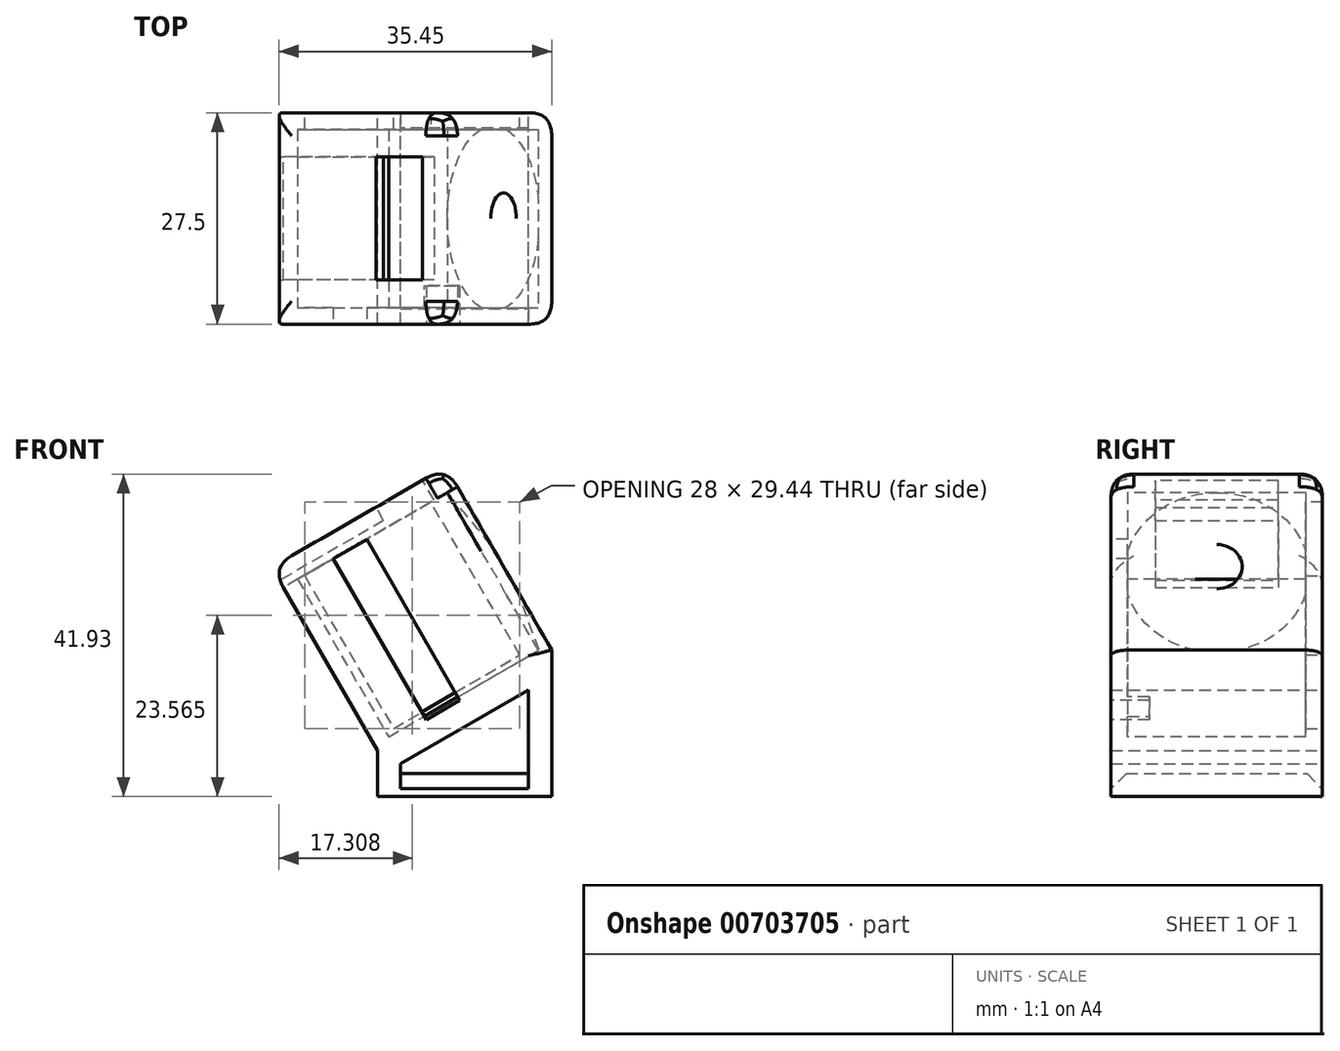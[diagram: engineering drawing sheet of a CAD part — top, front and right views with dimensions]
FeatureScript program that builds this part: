
annotation { "Feature Type Name" : "Feature", "Feature Type Description" : "" }
export const myFeature = defineFeature(function(context is Context, id is Id, definition is map)
    precondition{}
    {
        {
            var Q0;
            Q0=qCreatedBy(makeId("Front.planeOp"),FACE);
            var sketch = newSketch(context, id + "F0", { "sketchPlane" : qUnion([Q0])});
            skLineSegment(sketch, "E0", {"start": v(-14.45, -19.8) * mm, "end": v(8.2, -19.8) * mm});
            skLineSegment(sketch, "E1", {"start": v(-14.45, -19.8) * mm, "end": v(-14.45, -13.8) * mm});
            skLineSegment(sketch, "E2", {"start": v(-14.45, -13.8) * mm, "end": v(8.2, -0.73) * mm});
            skLineSegment(sketch, "E3", {"start": v(8.2, -0.73) * mm, "end": v(8.2, -19.8) * mm});
            skLineSegment(sketch, "E4", {"start": v(5.2, -16.8) * mm, "end": v(-11.45, -16.8) * mm});
            skPoint(sketch, "E4.startSnap0", {"position": v(-14.45, -16.8) * mm});
            skLineSegment(sketch, "E5", {"start": v(-11.45, -16.8) * mm, "end": v(-11.45, -15.53) * mm});
            skLineSegment(sketch, "E6", {"start": v(-11.45, -15.53) * mm, "end": v(5.2, -5.93) * mm});
            skLineSegment(sketch, "E7", {"start": v(5.2, -5.93) * mm, "end": v(5.2, -16.8) * mm});
            skLineSegment(sketch, "E8", {"start": v(-14.45, -13.8) * mm, "end": v(-28.2, 10.01) * mm});
            skLineSegment(sketch, "E9", {"start": v(-28.2, 10.01) * mm, "end": v(-5.55, 23.09) * mm});
            skLineSegment(sketch, "E10", {"start": v(-5.55, 23.09) * mm, "end": v(8.2, -0.73) * mm});
            skLineSegment(sketch, "E11", {"start": v(-28.2, 10.01) * mm, "end": v(-14.45, -13.8) * mm});
            skLineSegment(sketch, "E12", {"start": v(6.68, -1.6) * mm, "end": v(-15.88, -14.63) * mm});
            skSolve(sketch);
        }
        {
            var Q0;
            Q0 = qSketchRegion(id + "F0", true);
            extrude(context, id + "F1", {"entities" : qUnion([Q0]), "endBound" : BoundingType.SYMMETRIC, "depth" : 27.5 * mm, "offsetDistance" : 25 * mm});
        }
        {
            var Q0;
            Q0=qCreatedBy(makeId("Front.planeOp"),FACE);
            var sketch = newSketch(context, id + "F2", { "sketchPlane" : qUnion([Q0])});
            skLineSegment(sketch, "E13", {"start": v(-5.38, 19.72) * mm, "end": v(-24.86, 8.47) * mm});
            skLineSegment(sketch, "E14", {"start": v(-24.86, 8.47) * mm, "end": v(-13.01, -12.05) * mm});
            skLineSegment(sketch, "E15", {"start": v(8.3, 1.03) * mm, "end": v(8.3, 1.03) * mm});
            skLineSegment(sketch, "E16", {"start": v(-13.01, -12.05) * mm, "end": v(6.47, -0.8) * mm});
            skLineSegment(sketch, "E17", {"start": v(-5.38, 19.72) * mm, "end": v(6.47, -0.8) * mm});
            skSolve(sketch);
        }
        {
            var Q0;
            Q0 = qSketchRegion(id + "F2", true);
            extrude(context, id + "F3", {"entities" : qUnion([Q0]), "operationType" : NewBodyOperationType.REMOVE, "endBound" : BoundingType.SYMMETRIC, "oppositeDirection" : true, "depth" : 23.15 * mm, "offsetDistance" : 25 * mm});
        }
        {
            var Q0;
            Q0=makeQuery(id+"F1.opExtrude","SWEPT_FACE",FACE,{"disambiguationData":[OSD([sQuery(id+"F0.wireOp",EDGE,"E9")])]});
            var sketch = newSketch(context, id + "F4", { "sketchPlane" : qUnion([Q0])});
            skLineSegment(sketch, "E18", {"start": v(3.21, 8) * mm, "end": v(3.21, -8) * mm});
            skLineSegment(sketch, "E19", {"start": v(3.21, -8) * mm, "end": v(-3.79, -8) * mm});
            skLineSegment(sketch, "E20", {"start": v(-3.79, -8) * mm, "end": v(-3.79, 8) * mm});
            skLineSegment(sketch, "E21", {"start": v(-3.79, 8) * mm, "end": v(3.21, 8) * mm});
            skSolve(sketch);
        }
        {
            var Q0;
            Q0 = qSketchRegion(id + "F4", true);
            extrude(context, id + "F5", {"entities" : qUnion([Q0]), "operationType" : NewBodyOperationType.REMOVE, "oppositeDirection" : true, "depth" : 5 * mm, "offsetDistance" : 25 * mm});
        }
        {
            var Q0;
            Q0=makeQuery(id+"F1.opExtrude","CAP_FACE",FACE,{"disambiguationData":[OSD([sQuery(id+"F0.wireOp",EDGE,"E0"),sQuery(id+"F0.wireOp",EDGE,"E1"),sQuery(id+"F0.wireOp",EDGE,"E3"),sQuery(id+"F0.wireOp",EDGE,"E4"),sQuery(id+"F0.wireOp",EDGE,"E5"),sQuery(id+"F0.wireOp",EDGE,"E6"),sQuery(id+"F0.wireOp",EDGE,"E7"),sQuery(id+"F0.wireOp",EDGE,"E9"),sQuery(id+"F0.wireOp",EDGE,"E10"),sQuery(id+"F0.wireOp",EDGE,"E11")])],"isStart":false});
            var sketch = newSketch(context, id + "F6", { "sketchPlane" : qUnion([Q0])});
            skLineSegment(sketch, "E22", {"start": v(-20.2, 11.17) * mm, "end": v(-8.1, -9.8) * mm});
            skLineSegment(sketch, "E23", {"start": v(-8.1, -9.8) * mm, "end": v(-3.77, -7.3) * mm});
            skLineSegment(sketch, "E24", {"start": v(-3.77, -7.3) * mm, "end": v(-15.87, 13.67) * mm});
            skLineSegment(sketch, "E25", {"start": v(-15.87, 13.67) * mm, "end": v(-20.2, 11.17) * mm});
            skSolve(sketch);
        }
        {
            var Q0;
            Q0 = qSketchRegion(id + "F6", true);
            extrude(context, id + "F7", {"entities" : qUnion([Q0]), "operationType" : NewBodyOperationType.REMOVE, "oppositeDirection" : true, "depth" : 5 * mm, "offsetDistance" : 25 * mm});
        }
        {
            var Q0;
            Q0=makeQuery(id+"F5.boolean.opBoolean","COPY",EDGE,{"derivedFrom":makeQuery(id+"F5.opExtrude","CAP_EDGE",EDGE,{"disambiguationData":[OSD([sQuery(id+"F4.wireOp",EDGE,"E20")])],"isStart":true})});
            var Q1;
            Q1=makeQuery(id+"F5.boolean.opBoolean","COPY",EDGE,{"derivedFrom":makeQuery(id+"F5.opExtrude","CAP_EDGE",EDGE,{"disambiguationData":[OSD([sQuery(id+"F4.wireOp",EDGE,"E18")])],"isStart":true})});
            var Q2;
            Q2=makeQuery(id+"F5.boolean.opBoolean","COPY",EDGE,{"derivedFrom":makeQuery(id+"F5.opExtrude","CAP_EDGE",EDGE,{"disambiguationData":[OSD([sQuery(id+"F4.wireOp",EDGE,"E19")])],"isStart":true})});
            var Q3;
            Q3=makeQuery(id+"F5.boolean.opBoolean","COPY",EDGE,{"derivedFrom":makeQuery(id+"F5.opExtrude","CAP_EDGE",EDGE,{"disambiguationData":[OSD([sQuery(id+"F4.wireOp",EDGE,"E21")])],"isStart":true})});
            var Q4;
            Q4=makeQuery(id+"F7.boolean.opBoolean","COPY",EDGE,{"derivedFrom":makeQuery(id+"F7.opExtrude","CAP_EDGE",EDGE,{"disambiguationData":[OSD([sQuery(id+"F6.wireOp",EDGE,"E22")])],"isStart":true})});
            var Q5;
            Q5=makeQuery(id+"F7.boolean.opBoolean","COPY",EDGE,{"derivedFrom":makeQuery(id+"F7.opExtrude","CAP_EDGE",EDGE,{"disambiguationData":[OSD([sQuery(id+"F6.wireOp",EDGE,"E24")])],"isStart":true})});
            var Q6;
            Q6=makeQuery(id+"F1.opExtrude","CAP_EDGE",EDGE,{"disambiguationData":[OSD([sQuery(id+"F0.wireOp",EDGE,"E4")])],"isStart":false});
            var Q7;
            Q7=makeQuery(id+"F1.opExtrude","CAP_EDGE",EDGE,{"disambiguationData":[OSD([sQuery(id+"F0.wireOp",EDGE,"E4")])],"isStart":true});
            chamfer(context, id + "F8", {"entities" : qUnion([Q0, Q1, Q2, Q3, Q4, Q5, Q6, Q7]), "width" : 2 * mm, "tangentPropagation" : true});
        }
        {
            var Q0;
            Q0=makeQuery(id+"F7.boolean.opBoolean","MERGE",FACE,{"derivedFrom":[makeQuery(id+"F3.boolean.opBoolean","COPY",FACE,{"derivedFrom":makeQuery(id+"F3.opExtrude","SWEPT_FACE",FACE,{"disambiguationData":[OSD([sQuery(id+"F2.wireOp",EDGE,"E13")])]})}),makeQuery(id+"F7.opExtrude","SWEPT_FACE",FACE,{"disambiguationData":[OSD([sQuery(id+"F6.wireOp",EDGE,"E25")])]})]});
            var sketch = newSketch(context, id + "F9", { "sketchPlane" : qUnion([Q0])});
            skLineSegment(sketch, "E26", {"start": v(-3.79, 8) * mm, "end": v(-19.41, 8) * mm});
            skLineSegment(sketch, "E27", {"start": v(-3.79, -8) * mm, "end": v(-19.41, -8) * mm});
            skLineSegment(sketch, "E28", {"start": v(-19.41, -8) * mm, "end": v(-19.41, 8) * mm});
            skLineSegment(sketch, "E29", {"start": v(-3.79, 8) * mm, "end": v(-3.79, -8) * mm});
            skSolve(sketch);
        }
        {
            var Q0;
            Q0=makeQuery(id+"F9.imprint","IMPRINT",FACE,{"disambiguationData":[TD([[makeQuery(id+"F9.imprint","IMPRINT",EDGE,{"derivedFrom":sQuery(id+"F9.wireOp",EDGE,"E26")}),1.0]])]});
            extrude(context, id + "F10", {"entities" : qUnion([Q0]), "operationType" : NewBodyOperationType.REMOVE, "oppositeDirection" : true, "depth" : 1 * mm, "offsetDistance" : 25 * mm});
        }
        {
            var Q0;
            Q0=makeQuery(id+"F1.opExtrude","CAP_EDGE",EDGE,{"disambiguationData":[OSD([sQuery(id+"F0.wireOp",EDGE,"E10")])],"isStart":false});
            var Q1;
            Q1=makeQuery(id+"F1.opExtrude","CAP_EDGE",EDGE,{"disambiguationData":[OSD([sQuery(id+"F0.wireOp",EDGE,"E10")])],"isStart":true});
            var Q2;
            Q2=makeQuery(id+"F1.opExtrude","CAP_EDGE",EDGE,{"disambiguationData":[OSD([sQuery(id+"F0.wireOp",EDGE,"E9")])],"isStart":true});
            var Q3;
            Q3=makeQuery(id+"F1.opExtrude","CAP_EDGE",EDGE,{"disambiguationData":[OSD([sQuery(id+"F0.wireOp",EDGE,"E9")])],"isStart":false});
            var Q4;
            Q4=makeQuery(id+"F1.opExtrude","SWEPT_EDGE",EDGE,{"disambiguationData":[OSD([sQuery(id+"F0.wireOp",EDGE,"E9"),sQuery(id+"F0.wireOp",EDGE,"E10")])]});
            var Q5;
            Q5=makeQuery(id+"F1.opExtrude","SWEPT_EDGE",EDGE,{"disambiguationData":[OSD([sQuery(id+"F0.wireOp",EDGE,"E9"),sQuery(id+"F0.wireOp",EDGE,"E11")])]});
            var Q6;
            Q6=makeQuery(id+"F1.opExtrude","CAP_EDGE",EDGE,{"disambiguationData":[OSD([sQuery(id+"F0.wireOp",EDGE,"E11")])],"isStart":false});
            var Q7;
            Q7=makeQuery(id+"F1.opExtrude","CAP_EDGE",EDGE,{"disambiguationData":[OSD([sQuery(id+"F0.wireOp",EDGE,"E11")])],"isStart":true});
            var Q8;
            Q8=makeQuery(id+"F1.opExtrude","CAP_EDGE",EDGE,{"disambiguationData":[OSD([sQuery(id+"F0.wireOp",EDGE,"E3")])],"isStart":false});
            var Q9;
            Q9=makeQuery(id+"F1.opExtrude","CAP_EDGE",EDGE,{"disambiguationData":[OSD([sQuery(id+"F0.wireOp",EDGE,"E3")])],"isStart":true});
            fillet(context, id + "F11", {"entities" : qUnion([Q0, Q1, Q2, Q3, Q4, Q5, Q6, Q7, Q8, Q9]), "radius" : 3 * mm, "rho" : 0.5, "crossSection" : FilletCrossSection.CONIC, "allowEdgeOverflow" : false});
        }
        {
            var Q0;
            Q0=makeQuery(id+"F1.opExtrude","CAP_FACE",FACE,{"disambiguationData":[OSD([sQuery(id+"F0.wireOp",EDGE,"E0"),sQuery(id+"F0.wireOp",EDGE,"E1"),sQuery(id+"F0.wireOp",EDGE,"E3"),sQuery(id+"F0.wireOp",EDGE,"E4"),sQuery(id+"F0.wireOp",EDGE,"E5"),sQuery(id+"F0.wireOp",EDGE,"E6"),sQuery(id+"F0.wireOp",EDGE,"E7"),sQuery(id+"F0.wireOp",EDGE,"E9"),sQuery(id+"F0.wireOp",EDGE,"E10"),sQuery(id+"F0.wireOp",EDGE,"E11")])],"isStart":true});
            var sketch = newSketch(context, id + "F12", { "sketchPlane" : qUnion([Q0])});
            skLineSegment(sketch, "E30", {"start": v(7.53, 18.48) * mm, "end": v(-4.06, -1.39) * mm});
            skLineSegment(sketch, "E31", {"start": v(-4.06, -1.39) * mm, "end": v(12.36, -10.96) * mm});
            skLineSegment(sketch, "E32", {"start": v(12.36, -10.96) * mm, "end": v(23.94, 8.92) * mm});
            skLineSegment(sketch, "E33", {"start": v(23.94, 8.92) * mm, "end": v(7.53, 18.48) * mm});
            skSolve(sketch);
        }
        {
            var Q0;
            Q0 = qSketchRegion(id + "F12", true);
            extrude(context, id + "F13", {"entities" : qUnion([Q0]), "operationType" : NewBodyOperationType.REMOVE, "endBound" : BoundingType.SYMMETRIC, "oppositeDirection" : true, "depth" : 5 * mm, "offsetDistance" : 25 * mm});
        }
        {
            var Q0;
            Q0=makeQuery(id+"F1.opExtrude","SWEPT_FACE",FACE,{"disambiguationData":[OSD([sQuery(id+"F0.wireOp",EDGE,"E10")])]});
            var sketch = newSketch(context, id + "F14", { "sketchPlane" : qUnion([Q0])});
            skCircle(sketch, "E34", {"center": v(0, 7.77) * mm, "radius": 3 * mm});
            skSolve(sketch);
        }
        {
            var Q0;
            Q0=makeQuery(id+"F14.imprint","IMPRINT",FACE,{"disambiguationData":[TD([[makeQuery(id+"F14.imprint","IMPRINT",EDGE,{"derivedFrom":sQuery(id+"F14.wireOp",EDGE,"E34")}),1.0]])]});
            extrude(context, id + "F15", {"entities" : qUnion([Q0]), "operationType" : NewBodyOperationType.REMOVE, "endBound" : BoundingType.SYMMETRIC, "depth" : 5 * mm, "offsetDistance" : 25 * mm});
        }
        {
            var Q0;
            Q0=makeQuery(id+"F15.boolean.opBoolean","INTERSECT",EDGE,{"derivedFrom":[makeQuery(id+"F3.boolean.opBoolean","COPY",FACE,{"derivedFrom":makeQuery(id+"F3.opExtrude","SWEPT_FACE",FACE,{"disambiguationData":[OSD([sQuery(id+"F2.wireOp",EDGE,"E17")])]})}),makeQuery(id+"F15.opExtrude","SWEPT_FACE",FACE,{"disambiguationData":[OSD([sQuery(id+"F14.wireOp",EDGE,"E34")])]})]});
            chamfer(context, id + "F16", {"entities" : qUnion([Q0]), "chamferType" : ChamferType.OFFSET_ANGLE, "width" : 9 * mm, "oppositeDirection" : false, "angle" : 10 * degree, "tangentPropagation" : true});
        }
    });
